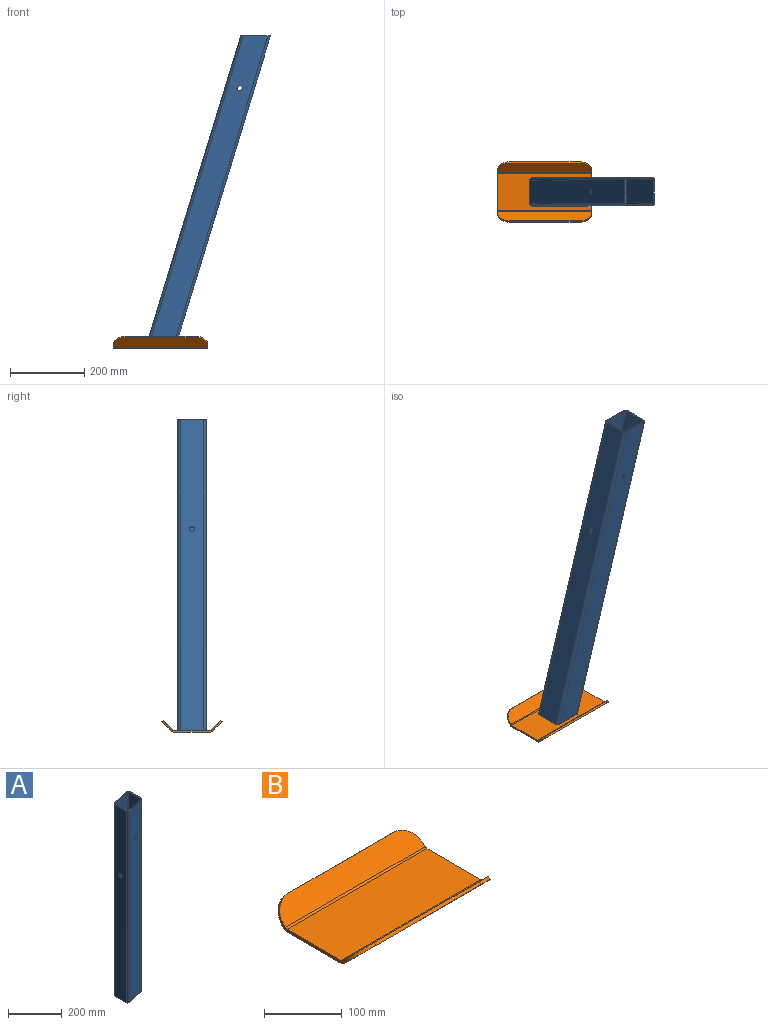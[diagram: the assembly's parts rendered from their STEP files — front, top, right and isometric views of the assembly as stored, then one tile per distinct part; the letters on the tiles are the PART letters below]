
ASSEMBLY  parts=2 mates=1
PART A: 22 faces, bbox 76.2x76.2x897.1 mm
  f0: cylinder r=3.3mm len=874.76mm, axis (0,0,-1), area 4532mm2, adj f1,f7,f8,f9
  f1: plane 873.76x63.5mm, normal (-1,0,0), area 55322.8mm2, adj f0,f2,f8,f9,f21
  f2: cylinder r=3.3mm len=874.76mm, axis (0,0,-1), area 4532mm2, adj f1,f3,f8,f9
  f3: plane 893.17x63.5mm, normal (0,1,0), area 55322.8mm2, adj f2,f4,f8,f9,f11
  f4: cylinder r=3.3mm len=874.76mm, axis (0,0,-1), area 4532mm2, adj f3,f5,f8,f9
  f5: plane 873.76x63.5mm, normal (1,0,0), area 55322.8mm2, adj f4,f6,f8,f9,f20
  f6: cylinder r=3.3mm len=874.76mm, axis (0,0,-1), area 4532mm2, adj f5,f7,f8,f9
  f7: plane 893.17x63.5mm, normal (0,-1,0), area 55322.8mm2, adj f0,f6,f8,f9,f10
  f8: plane 76.2x76.2mm, normal (0.29,0,-0.96), area 906.2mm2, adj f0,f1,f2,f3,f4,f5,f6,f7
  f9: plane 76.2x76.2mm, normal (-0.29,0,0.96), area 906.2mm2, adj f0,f1,f2,f3,f4,f5,f6,f7
  f10: cylinder r=7.15mm len=14.3mm, axis (0,-1,0), area 136.9mm2, adj f7,f17
  f11: cylinder r=7.15mm len=14.3mm, axis (0,-1,0), area 136.9mm2, adj f3,f13
  f12: cylinder r=6.35mm len=875.7mm, axis (0,0,-1), area 8715.3mm2, adj f8,f9,f13,f18
  f13: plane 893.17x63.5mm, normal (0,-1,0), area 55322.8mm2, adj f8,f9,f11,f12,f14
  f14: cylinder r=6.35mm len=875.7mm, axis (0,0,-1), area 8715.3mm2, adj f8,f9,f13,f19
  f15: cylinder r=6.35mm len=875.7mm, axis (0,0,-1), area 8715.3mm2, adj f8,f9,f17,f18
  f16: cylinder r=6.35mm len=875.7mm, axis (0,0,-1), area 8715.3mm2, adj f8,f9,f17,f19
  f17: plane 893.17x63.5mm, normal (0,1,0), area 55322.8mm2, adj f8,f9,f10,f15,f16
  f18: plane 873.76x63.5mm, normal (1,0,0), area 55322.8mm2, adj f8,f9,f12,f15,f21
  f19: plane 873.76x63.5mm, normal (-1,0,0), area 55322.8mm2, adj f8,f9,f14,f16,f20
  f20: cylinder r=7.15mm len=14.3mm, axis (1,0,0), area 136.9mm2, adj f5,f19
  f21: cylinder r=7.15mm len=14.3mm, axis (1,0,0), area 136.9mm2, adj f1,f18
PART B: 26 faces, bbox 254x162x31.6 mm
  f0: plane 97.65x4.55mm, normal (-1,0,0), area 444mm2, adj f2,f3,f12,f23
  f1: plane 97.65x4.55mm, normal (1,0,0), area 444mm2, adj f2,f3,f11,f22
  f2: plane 254x97.65mm, normal (0,0,-1), area 24804.3mm2, adj f0,f1,f13,f24
  f3: plane 254x97.65mm, normal (0,0,1), area 24804.3mm2, adj f0,f1,f14,f25
  f4: plane 6.38x6.38mm, normal (-1,0,0), area 20.3mm2, adj f7,f8,f9,f12
  f5: plane 190.5x3.22mm, normal (0,0.71,0.71), area 866.1mm2, adj f7,f8,f9,f10
  f6: plane 6.38x6.38mm, normal (1,0,0), area 20.3mm2, adj f7,f8,f10,f11
  f7: plane 254x25.61mm, normal (0,0.71,-0.71), area 8767.6mm2, adj f4,f5,f6,f9,f10,f13
  f8: plane 254x25.61mm, normal (0,-0.71,0.71), area 8767.6mm2, adj f4,f5,f6,f9,f10,f14
  f9: cylinder r=31.75mm len=31.75mm, axis (0,-0.71,0.71), area 226.8mm2, adj f4,f5,f7,f8
  f10: cylinder r=31.75mm len=31.75mm, axis (0,0.71,-0.71), area 226.8mm2, adj f5,f6,f7,f8
  f11: plane 6.58x5.94mm, normal (1,0,0), area 25.1mm2, adj f1,f6,f13,f14
  f12: plane 6.58x5.94mm, normal (-1,0,0), area 25.1mm2, adj f0,f4,f13,f14
  f13: cylinder r=9.31mm len=254mm, axis (1,0,0), area 1857.1mm2, adj f2,f7,f11,f12
  f14: cylinder r=4.76mm len=254mm, axis (1,0,0), area 950.1mm2, adj f3,f8,f11,f12
  f15: plane 6.38x6.38mm, normal (-1,0,0), area 20.3mm2, adj f18,f19,f21,f23
  f16: plane 6.38x6.38mm, normal (1,0,0), area 20.3mm2, adj f18,f19,f20,f22
  f17: plane 190.5x3.22mm, normal (0,-0.71,0.71), area 866.1mm2, adj f18,f19,f20,f21
  f18: plane 254x25.61mm, normal (0,-0.71,-0.71), area 8767.6mm2, adj f15,f16,f17,f20,f21,f24
  f19: plane 254x25.61mm, normal (0,0.71,0.71), area 8767.6mm2, adj f15,f16,f17,f20,f21,f25
  f20: cylinder r=31.75mm len=31.75mm, axis (0,-0.71,-0.71), area 226.8mm2, adj f16,f17,f18,f19
  f21: cylinder r=31.75mm len=31.75mm, axis (0,0.71,0.71), area 226.8mm2, adj f15,f17,f18,f19
  f22: plane 6.58x5.94mm, normal (1,0,0), area 25.1mm2, adj f1,f16,f24,f25
  f23: plane 6.58x5.94mm, normal (-1,0,0), area 25.1mm2, adj f0,f15,f24,f25
  f24: cylinder r=9.31mm len=254mm, axis (1,0,0), area 1857.1mm2, adj f2,f18,f22,f23
  f25: cylinder r=4.76mm len=254mm, axis (1,0,0), area 950.1mm2, adj f3,f19,f22,f23
PLACE A rot(axis=(0,1,0),17deg) t=(144.12,-250.01,17.35)mm
PLACE B t=(143.39,-250.01,-400.44)mm fixed
MATE planar B.f3 <-> A.f8  axis (0,0,1) through (16.39,-250.01,-400.44)mm
